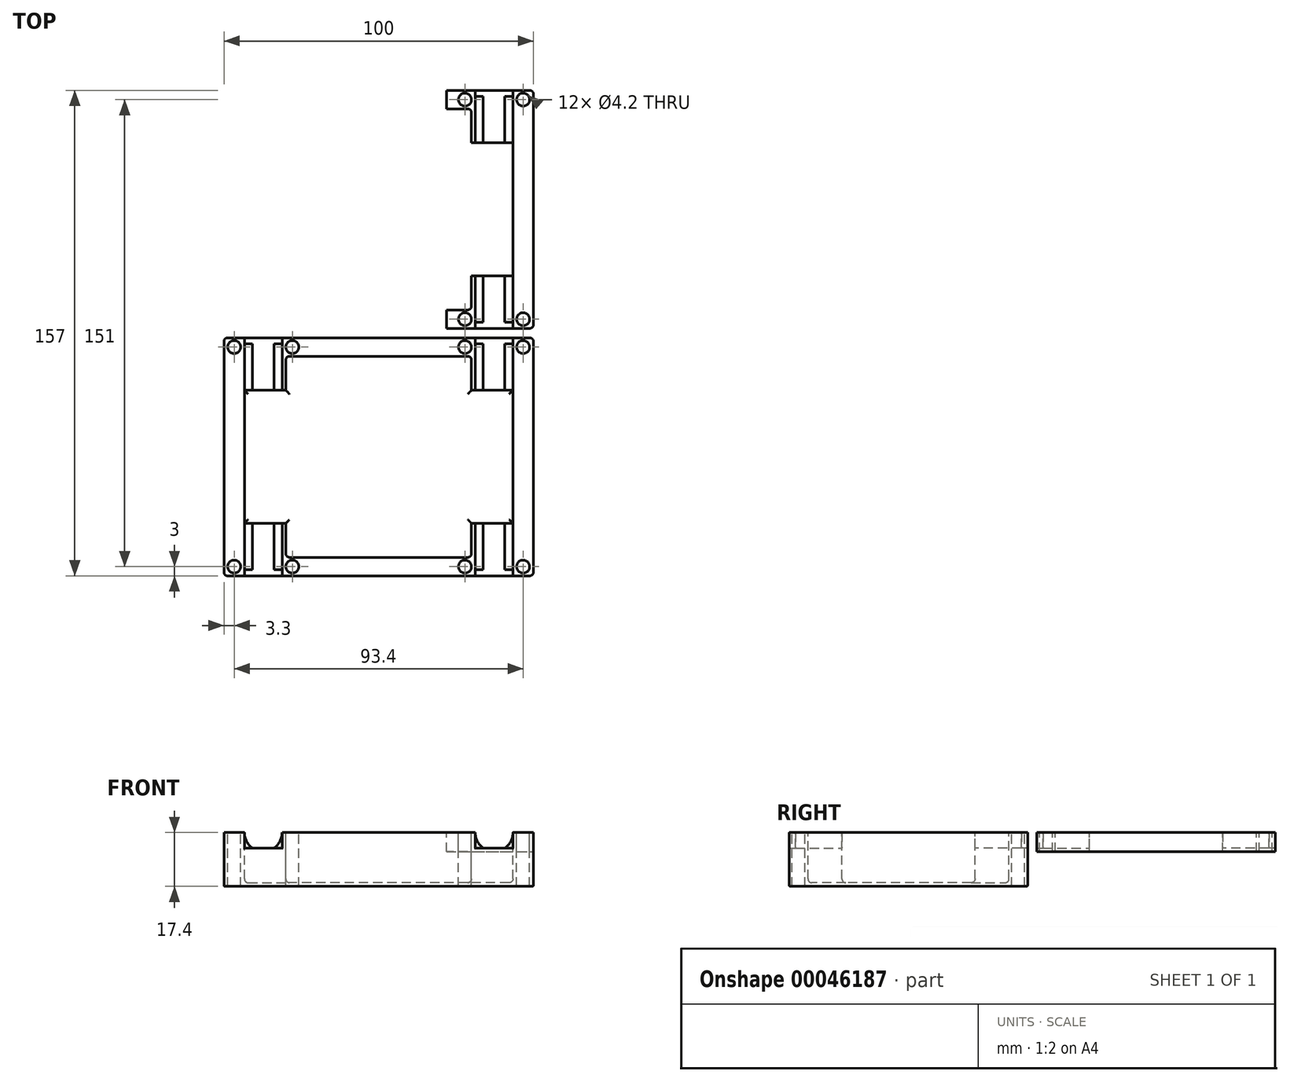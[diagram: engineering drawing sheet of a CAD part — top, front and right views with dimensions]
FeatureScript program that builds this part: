
annotation { "Feature Type Name" : "Feature", "Feature Type Description" : "" }
export const myFeature = defineFeature(function(context is Context, id is Id, definition is map)
    precondition{}
    {
        {
            var Q0;
            Q0=qCreatedBy(makeId("Top.planeOp"),FACE);
            var sketch = newSketch(context, id + "F0", { "sketchPlane" : qUnion([Q0])});
            skLineSegment(sketch, "E0.bottom", {"start": v(0, 0) * mm, "end": v(-30, 0) * mm});
            skLineSegment(sketch, "E0.top", {"start": v(0, 32.5) * mm, "end": v(-30, 32.5) * mm});
            skLineSegment(sketch, "E0.left", {"start": v(0, 0) * mm, "end": v(0, 32.5) * mm});
            skLineSegment(sketch, "E0.right", {"start": v(-30, 0) * mm, "end": v(-30, 32.5) * mm});
            skLineSegment(sketch, "E1", {"start": v(0, 32.5) * mm, "end": v(0, 38.5) * mm});
            skLineSegment(sketch, "E2", {"start": v(0, 38.5) * mm, "end": v(-50, 38.5) * mm});
            skLineSegment(sketch, "E3", {"start": v(-50, 38.5) * mm, "end": v(-50, 0) * mm});
            skLineSegment(sketch, "E4", {"start": v(-50, 0) * mm, "end": v(-30, 0) * mm});
            skLineSegment(sketch, "E5", {"start": v(-30, 32.5) * mm, "end": v(-30, 38.5) * mm});
            skLineSegment(sketch, "E6", {"start": v(-31.2, 38.5) * mm, "end": v(-31.2, 0) * mm});
            skLineSegment(sketch, "E7", {"start": v(-43.4, 38.5) * mm, "end": v(-43.4, 0) * mm});
            skLineSegment(sketch, "E8.bottom", {"start": v(-43.4, 36.5) * mm, "end": v(-31.2, 36.5) * mm});
            skLineSegment(sketch, "E8.top", {"start": v(-43.4, 21.5) * mm, "end": v(-31.2, 21.5) * mm});
            skLineSegment(sketch, "E8.left", {"start": v(-43.4, 36.5) * mm, "end": v(-43.4, 21.5) * mm});
            skLineSegment(sketch, "E8.right", {"start": v(-31.2, 36.5) * mm, "end": v(-31.2, 21.5) * mm});
            skLineSegment(sketch, "E9", {"start": v(-27.9, 38.5) * mm, "end": v(-27.9, 32.5) * mm, "construction": true});
            skCircle(sketch, "E10", {"center": v(-27.9, 35.5) * mm, "radius": 2.1 * mm});
            skLineSegment(sketch, "E11", {"start": v(-27.9, 35.5) * mm, "end": v(-50, 35.5) * mm, "construction": true});
            skLineSegment(sketch, "E12", {"start": v(-46.7, 38.5) * mm, "end": v(-46.7, 35.5) * mm, "construction": true});
            skCircle(sketch, "E13", {"center": v(-46.7, 35.5) * mm, "radius": 2.1 * mm});
            skSolve(sketch);
        }
        {
            var Q0;
            {var subQ1=sQuery(id+"F0.wireOp",EDGE,"E0.top");Q0=makeQuery(id+"F0.imprint","IMPRINT",FACE,{"disambiguationData":[TD([[makeQuery(id+"F0.imprint","IMPRINT",EDGE,{"derivedFrom":subQ1}),-1.0]])]});}
            var Q1;
            Q1=makeQuery(id+"F0.imprint","IMPRINT",FACE,{"disambiguationData":[TD([[makeQuery(id+"F0.imprint","IMPRINT",EDGE,{"derivedFrom":sQuery(id+"F0.wireOp",EDGE,"E0.bottom")}),-1.0]])]});
            var Q2;
            {var subQ5=sQuery(id+"F0.wireOp",EDGE,"E8.top");Q2=makeQuery(id+"F0.imprint","IMPRINT",FACE,{"disambiguationData":[TD([[makeQuery(id+"F0.imprint","IMPRINT",EDGE,{"derivedFrom":subQ5}),-1.0]])]});}
            var Q3;
            {var subQ5=sQuery(id+"F0.wireOp",EDGE,"E3");Q3=makeQuery(id+"F0.imprint","IMPRINT",FACE,{"disambiguationData":[TD([[makeQuery(id+"F0.imprint","IMPRINT",EDGE,{"derivedFrom":subQ5}),1.0]])]});}
            var Q4;
            Q4=makeQuery(id+"F0.imprint","IMPRINT",FACE,{"disambiguationData":[TD([[makeQuery(id+"F0.imprint","IMPRINT",EDGE,{"derivedFrom":sQuery(id+"F0.wireOp",EDGE,"E8.bottom")}),-1.0]])]});
            var Q5;
            {var subQ5=sQuery(id+"F0.wireOp",EDGE,"E8.bottom");Q5=makeQuery(id+"F0.imprint","IMPRINT",FACE,{"disambiguationData":[TD([[makeQuery(id+"F0.imprint","IMPRINT",EDGE,{"derivedFrom":subQ5}),1.0]])]});}
            var Q6;
            {var subQ1=sQuery(id+"F0.wireOp",EDGE,"E0.right");Q6=makeQuery(id+"F0.imprint","IMPRINT",FACE,{"disambiguationData":[TD([[makeQuery(id+"F0.imprint","IMPRINT",EDGE,{"derivedFrom":subQ1}),1.0]])]});}
            extrude(context, id + "F1", {"entities" : qUnion([Q0, Q1, Q2, Q3, Q4, Q5, Q6]), "oppositeDirection" : true, "depth" : 12.4 * mm});
        }
        {
            var Q0;
            Q0=makeQuery(id+"F0.imprint","IMPRINT",FACE,{"disambiguationData":[TD([[makeQuery(id+"F0.imprint","IMPRINT",EDGE,{"derivedFrom":sQuery(id+"F0.wireOp",EDGE,"E0.bottom")}),-1.0]])]});
            var Q1;
            {var subQ5=sQuery(id+"F0.wireOp",EDGE,"E8.top");Q1=makeQuery(id+"F0.imprint","IMPRINT",FACE,{"disambiguationData":[TD([[makeQuery(id+"F0.imprint","IMPRINT",EDGE,{"derivedFrom":subQ5}),-1.0]])]});}
            extrude(context, id + "F2", {"entities" : qUnion([Q0, Q1]), "operationType" : NewBodyOperationType.REMOVE, "oppositeDirection" : true, "depth" : 11.2 * mm});
        }
        {
            var Q0;
            {var subQ1=sQuery(id+"F0.wireOp",EDGE,"E0.top");Q0=makeQuery(id+"F0.imprint","IMPRINT",FACE,{"disambiguationData":[TD([[makeQuery(id+"F0.imprint","IMPRINT",EDGE,{"derivedFrom":subQ1}),-1.0]])]});}
            var Q1;
            {var subQ1=sQuery(id+"F0.wireOp",EDGE,"E0.right");Q1=makeQuery(id+"F0.imprint","IMPRINT",FACE,{"disambiguationData":[TD([[makeQuery(id+"F0.imprint","IMPRINT",EDGE,{"derivedFrom":subQ1}),1.0]])]});}
            var Q2;
            {var subQ5=sQuery(id+"F0.wireOp",EDGE,"E3");Q2=makeQuery(id+"F0.imprint","IMPRINT",FACE,{"disambiguationData":[TD([[makeQuery(id+"F0.imprint","IMPRINT",EDGE,{"derivedFrom":subQ5}),1.0]])]});}
            extrude(context, id + "F3", {"entities" : qUnion([Q0, Q1, Q2]), "operationType" : NewBodyOperationType.ADD, "depth" : 5 * mm});
        }
        {
            var Q0;
            {var subQ0=sQuery(id+"F0.wireOp",EDGE,"E6");Q0=makeQuery(id+"F3.boolean.opBoolean","MERGE",FACE,{"derivedFrom":[makeQuery(id+"F2.boolean.opBoolean","COPY",FACE,{"derivedFrom":makeQuery(id+"F2.opExtrude","SWEPT_FACE",FACE,{"disambiguationData":[OSD([subQ0])]})}),makeQuery(id+"F3.opExtrude","SWEPT_FACE",FACE,{"disambiguationData":[OSD([subQ0,sQuery(id+"F0.wireOp",EDGE,"E8.right")])]})]});}
            var sketch = newSketch(context, id + "F4", { "sketchPlane" : qUnion([Q0])});
            skLineSegment(sketch, "E14", {"start": v(-21.5, -11.2) * mm, "end": v(-21.5, 5) * mm});
            skSolve(sketch);
        }
        {
            var Q0;
            {var subQ2=sQuery(id+"F0.wireOp",EDGE,"E6");var subQ8=makeQuery(id+"F2.boolean.opBoolean","COPY",EDGE,{"derivedFrom":makeQuery(id+"F2.opExtrude","CAP_EDGE",EDGE,{"disambiguationData":[OSD([subQ2])],"isStart":false})});Q0=makeQuery(id+"F4.imprint","IMPRINT",FACE,{"disambiguationData":[TD([[makeQuery(id+"F4.imprint","IMPRINT",EDGE,{"derivedFrom":subQ8}),1.0]])]});}
            extrude(context, id + "F5", {"entities" : qUnion([Q0]), "operationType" : NewBodyOperationType.REMOVE, "endBound" : BoundingType.UP_TO_NEXT, "oppositeDirection" : true, "depth" : 25 * mm});
        }
        {
            var Q0;
            Q0=makeQuery(id+"F5.boolean.opBoolean","MERGE",FACE,{"derivedFrom":[makeQuery(id+"F2.boolean.opBoolean","COPY",FACE,{"derivedFrom":makeQuery(id+"F2.opExtrude","SWEPT_FACE",FACE,{"disambiguationData":[OSD([sQuery(id+"F0.wireOp",EDGE,"E8.top")])]})}),makeQuery(id+"F5.opExtrude","SWEPT_FACE",FACE,{"disambiguationData":[OSD([sQuery(id+"F4.wireOp",EDGE,"E14")])]})]});
            var sketch = newSketch(context, id + "F6", { "sketchPlane" : qUnion([Q0])});
            skLineSegment(sketch, "E15.0", {"start": v(-43.4, -11.2) * mm, "end": v(-43.4, 5) * mm, "construction": true});
            skLineSegment(sketch, "E16.0", {"start": v(-31.2, 0) * mm, "end": v(-31.2, 5) * mm, "construction": true});
            skLineSegment(sketch, "E17", {"start": v(-43.4, 5) * mm, "end": v(-31.2, 5) * mm, "construction": true});
            skArc(sketch, "E18", {"start": v(-43.4, 5) * mm, "mid": v(-42.7, 2.18) * mm, "end": v(-40.8, 0) * mm});
            skLineSegment(sketch, "E19.0", {"start": v(-43.4, 0) * mm, "end": v(-31.2, 0) * mm});
            skArc(sketch, "E20.trimOffspring", {"start": v(-33.8, 0) * mm, "mid": v(-31.9, 2.18) * mm, "end": v(-31.2, 5) * mm});
            skLineSegment(sketch, "E21", {"start": v(-43.4, 0) * mm, "end": v(-43.4, 5) * mm});
            skLineSegment(sketch, "E22", {"start": v(-31.2, 5) * mm, "end": v(-31.2, 0) * mm});
            skSolve(sketch);
        }
        {
            var Q0;
            {var subQ2=sQuery(id+"F6.wireOp",EDGE,"E20.trimOffspring");Q0=makeQuery(id+"F6.imprint","IMPRINT",FACE,{"disambiguationData":[TD([[makeQuery(id+"F6.imprint","IMPRINT",EDGE,{"derivedFrom":subQ2}),-1.0]])]});}
            var Q1;
            {var subQ0=sQuery(id+"F6.wireOp",EDGE,"E18");Q1=makeQuery(id+"F6.imprint","IMPRINT",FACE,{"disambiguationData":[TD([[makeQuery(id+"F6.imprint","IMPRINT",EDGE,{"derivedFrom":subQ0}),-1.0]])]});}
            extrude(context, id + "F7", {"entities" : qUnion([Q0, Q1]), "operationType" : NewBodyOperationType.ADD, "oppositeDirection" : true, "depth" : 15 * mm});
        }
        {
            var Q0;
            Q0=makeQuery(id+"F2.boolean.opBoolean","COPY",EDGE,{"derivedFrom":makeQuery(id+"F2.opExtrude","CAP_EDGE",EDGE,{"disambiguationData":[OSD([sQuery(id+"F0.wireOp",EDGE,"E7")])],"isStart":false})});
            var Q1;
            {var subQ0=sQuery(id+"F0.wireOp",EDGE,"E8.top");Q1=makeQuery(id+"F5.boolean.opBoolean","MERGE",EDGE,{"derivedFrom":[makeQuery(id+"F2.boolean.opBoolean","COPY",EDGE,{"derivedFrom":makeQuery(id+"F2.opExtrude","CAP_EDGE",EDGE,{"disambiguationData":[OSD([subQ0])],"isStart":false})}),makeQuery(id+"F5.opExtrude","SWEPT_EDGE",EDGE,{"disambiguationData":[OSD([sQuery(id+"F0.wireOp",EDGE,"E6"),subQ0,sQuery(id+"F0.wireOp",EDGE,"E8.right"),sQuery(id+"F4.wireOp",EDGE,"E14")])]})]});}
            var Q2;
            {var subQ0=sQuery(id+"F0.wireOp",EDGE,"E5");var subQ1=sQuery(id+"F0.wireOp",EDGE,"E0.right");var subQ2=sQuery(id+"F0.wireOp",EDGE,"E0.top");Q2=makeQuery(id+"F3.boolean.opBoolean","MERGE",EDGE,{"derivedFrom":[makeQuery(id+"F2.boolean.opBoolean","COPY",EDGE,{"derivedFrom":makeQuery(id+"F2.opExtrude","SWEPT_EDGE",EDGE,{"disambiguationData":[OSD([subQ2,subQ1,subQ0])]})}),makeQuery(id+"F3.opExtrude","SWEPT_EDGE",EDGE,{"disambiguationData":[OSD([subQ2,subQ1,subQ0])]})]});}
            var Q3;
            {var subQ0=sQuery(id+"F0.wireOp",EDGE,"E3");var subQ1=sQuery(id+"F0.wireOp",EDGE,"E2");Q3=makeQuery(id+"F3.boolean.opBoolean","MERGE",EDGE,{"derivedFrom":[makeQuery(id+"F1.opExtrude","SWEPT_EDGE",EDGE,{"disambiguationData":[OSD([subQ1,subQ0])]}),makeQuery(id+"F3.opExtrude","SWEPT_EDGE",EDGE,{"disambiguationData":[OSD([subQ1,subQ0])]})]});}
            var Q4;
            Q4=makeQuery(id+"F2.boolean.opBoolean","COPY",EDGE,{"derivedFrom":makeQuery(id+"F2.opExtrude","CAP_EDGE",EDGE,{"disambiguationData":[OSD([sQuery(id+"F0.wireOp",EDGE,"E0.right")])],"isStart":false})});
            var Q5;
            Q5=makeQuery(id+"F2.boolean.opBoolean","COPY",EDGE,{"derivedFrom":makeQuery(id+"F2.opExtrude","CAP_EDGE",EDGE,{"disambiguationData":[OSD([sQuery(id+"F0.wireOp",EDGE,"E0.top")])],"isStart":false})});
            fillet(context, id + "F8", {"entities" : qUnion([Q0, Q1, Q2, Q3, Q4, Q5]), "radius" : 1.2 * mm, "tangentPropagation" : true, "allowEdgeOverflow" : false});
        }
        {
            var Q0;
            Q0=makeQuery(id+"F1.opExtrude","CAP_EDGE",EDGE,{"disambiguationData":[OSD([sQuery(id+"F0.wireOp",EDGE,"E3")])],"isStart":false});
            var Q1;
            Q1=makeQuery(id+"F3.opExtrude","SWEPT_EDGE",EDGE,{"disambiguationData":[OSD([sQuery(id+"F0.wireOp",EDGE,"E2"),sQuery(id+"F0.wireOp",EDGE,"E6")])]});
            var Q2;
            Q2=makeQuery(id+"F3.opExtrude","SWEPT_EDGE",EDGE,{"disambiguationData":[OSD([sQuery(id+"F0.wireOp",EDGE,"E2"),sQuery(id+"F0.wireOp",EDGE,"E7")])]});
            fillet(context, id + "F9", {"entities" : qUnion([Q0, Q1, Q2]), "radius" : .3 * mm, "tangentPropagation" : true, "allowEdgeOverflow" : false});
        }
        {
            var Q0;
            Q0=makeQuery(id+"F1.opExtrude","SWEPT_BODY",BODY,{"disambiguationData":[OSD([sQuery(id+"F0.wireOp",EDGE,"E0.bottom"),sQuery(id+"F0.wireOp",EDGE,"E0.left"),sQuery(id+"F0.wireOp",EDGE,"E1"),sQuery(id+"F0.wireOp",EDGE,"E2"),sQuery(id+"F0.wireOp",EDGE,"E3"),sQuery(id+"F0.wireOp",EDGE,"E4"),sQuery(id+"F0.wireOp",EDGE,"E10"),sQuery(id+"F0.wireOp",EDGE,"E13")])]});
            var Q1;
            {var subQ0=sQuery(id+"F0.wireOp",EDGE,"E4");var subQ1=sQuery(id+"F0.wireOp",EDGE,"E0.bottom");Q1=makeQuery(id+"F3.boolean.opBoolean","MERGE",FACE,{"derivedFrom":[makeQuery(id+"F1.opExtrude","SWEPT_FACE",FACE,{"disambiguationData":[OSD([subQ1,subQ0])]}),makeQuery(id+"F3.opExtrude","SWEPT_FACE",FACE,{"disambiguationData":[OSD([subQ0]),TDD([makeQuery(id+"F0.imprint","IMPRINT",EDGE,{"disambiguationData":[TD([[makeQuery(id+"F0.imprint","INTERSECT",VERTEX,{"derivedFrom":[sQuery(id+"F0.wireOp",EDGE,"E3"),subQ0]}),-1.0]])],"derivedFrom":subQ0})])]}),makeQuery(id+"F3.opExtrude","SWEPT_FACE",FACE,{"disambiguationData":[OSD([subQ0]),TDD([makeQuery(id+"F0.imprint","IMPRINT",EDGE,{"disambiguationData":[TD([[makeQuery(id+"F0.imprint","INTERSECT",VERTEX,{"derivedFrom":[subQ0,sQuery(id+"F0.wireOp",EDGE,"E6")]}),-1.0]])],"derivedFrom":subQ0})])]})]});}
            mirror(context, id + "F10", {"operationType" : NewBodyOperationType.ADD, "entities" : qUnion([Q0]), "mirrorPlane" : qUnion([Q1])});
        }
        {
            var Q0;
            Q0=makeQuery(id+"F1.opExtrude","SWEPT_BODY",BODY,{"disambiguationData":[OSD([sQuery(id+"F0.wireOp",EDGE,"E0.bottom"),sQuery(id+"F0.wireOp",EDGE,"E0.left"),sQuery(id+"F0.wireOp",EDGE,"E1"),sQuery(id+"F0.wireOp",EDGE,"E2"),sQuery(id+"F0.wireOp",EDGE,"E3"),sQuery(id+"F0.wireOp",EDGE,"E4"),sQuery(id+"F0.wireOp",EDGE,"E10"),sQuery(id+"F0.wireOp",EDGE,"E13")])]});
            var Q1;
            {var subQ0=sQuery(id+"F0.wireOp",EDGE,"E1");var subQ1=makeQuery(id+"F3.boolean.opBoolean","MERGE",FACE,{"derivedFrom":[makeQuery(id+"F1.opExtrude","SWEPT_FACE",FACE,{"disambiguationData":[OSD([sQuery(id+"F0.wireOp",EDGE,"E0.left"),subQ0])]}),makeQuery(id+"F3.opExtrude","SWEPT_FACE",FACE,{"disambiguationData":[OSD([subQ0])]})]});Q1=makeQuery(id+"F10.boolean.opBoolean","MERGE",FACE,{"derivedFrom":[subQ1,makeQuery(id+"F10.opPattern","COPY",FACE,{"derivedFrom":subQ1,"instanceName":"1"})]});}
            mirror(context, id + "F11", {"operationType" : NewBodyOperationType.ADD, "entities" : qUnion([Q0]), "mirrorPlane" : qUnion([Q1])});
        }
        {
            var Q0;
            Q0=makeQuery(id+"F1.opExtrude","SWEPT_BODY",BODY,{"disambiguationData":[OSD([sQuery(id+"F0.wireOp",EDGE,"E0.bottom"),sQuery(id+"F0.wireOp",EDGE,"E0.left"),sQuery(id+"F0.wireOp",EDGE,"E1"),sQuery(id+"F0.wireOp",EDGE,"E2"),sQuery(id+"F0.wireOp",EDGE,"E3"),sQuery(id+"F0.wireOp",EDGE,"E4"),sQuery(id+"F0.wireOp",EDGE,"E10"),sQuery(id+"F0.wireOp",EDGE,"E13")])]});
            transform(context, id + "F12", {"entities" : qUnion([Q0]), "transformType" : TransformType.TRANSLATION_3D, "dx" : 0 * mm, "dy" : 80 * mm, "dz" : 0 * mm, "makeCopy" : true});
        }
        {
            var Q0;
            {var subQ0=sQuery(id+"F0.wireOp",EDGE,"E2");var subQ1=makeQuery(id+"F0.imprint","INTERSECT",VERTEX,{"derivedFrom":[subQ0,sQuery(id+"F0.wireOp",EDGE,"E5")]});var subQ2=makeQuery(id+"F10.opPattern","COPY",FACE,{"derivedFrom":makeQuery(id+"F3.boolean.opBoolean","MERGE",FACE,{"derivedFrom":[makeQuery(id+"F1.opExtrude","SWEPT_FACE",FACE,{"disambiguationData":[OSD([subQ0])]}),makeQuery(id+"F3.opExtrude","SWEPT_FACE",FACE,{"disambiguationData":[OSD([subQ0]),TDD([makeQuery(id+"F0.imprint","IMPRINT",EDGE,{"disambiguationData":[TD([[makeQuery(id+"F0.imprint","INTERSECT",VERTEX,{"derivedFrom":[sQuery(id+"F0.wireOp",EDGE,"E1"),subQ0]}),-1.0]])],"derivedFrom":subQ0}),makeQuery(id+"F0.imprint","IMPRINT",EDGE,{"disambiguationData":[TD([[subQ1,-1.0]])],"derivedFrom":subQ0})])]}),makeQuery(id+"F3.opExtrude","SWEPT_FACE",FACE,{"disambiguationData":[OSD([subQ0]),TDD([makeQuery(id+"F0.imprint","IMPRINT",EDGE,{"disambiguationData":[TD([[makeQuery(id+"F0.imprint","INTERSECT",VERTEX,{"derivedFrom":[subQ0,sQuery(id+"F0.wireOp",EDGE,"E3")]}),1.0]])],"derivedFrom":subQ0})])]})]}),"instanceName":"1"});Q0=makeQuery(id+"F12.opPattern","COPY",FACE,{"derivedFrom":makeQuery(id+"F11.boolean.opBoolean","MERGE",FACE,{"derivedFrom":[subQ2,makeQuery(id+"F11.opPattern","COPY",FACE,{"derivedFrom":subQ2,"instanceName":"1"})]}),"instanceName":"1"});}
            var sketch = newSketch(context, id + "F13", { "sketchPlane" : qUnion([Q0])});
            skLineSegment(sketch, "E23.0", {"start": v(50, 5) * mm, "end": v(50, -12.1) * mm});
            skLineSegment(sketch, "E24.0", {"start": v(-48.8, -12.4) * mm, "end": v(48.8, -12.4) * mm});
            skLineSegment(sketch, "E25", {"start": v(22, -1.2) * mm, "end": v(50, -1.2) * mm});
            skLineSegment(sketch, "E26", {"start": v(22, -1.2) * mm, "end": v(22, -12.4) * mm});
            skLineSegment(sketch, "E27", {"start": v(22, -12.4) * mm, "end": v(50, -12.4) * mm});
            skLineSegment(sketch, "E28", {"start": v(50, -12.4) * mm, "end": v(50, -12.1) * mm});
            skLineSegment(sketch, "E29.0", {"start": v(30.9, 0) * mm, "end": v(43.7, 0) * mm});
            skLineSegment(sketch, "E30", {"start": v(22, -1.2) * mm, "end": v(22, 5) * mm});
            skLineSegment(sketch, "E31.0", {"start": v(-50, 5) * mm, "end": v(-50, -12.1) * mm});
            skLineSegment(sketch, "E32", {"start": v(-50, 5) * mm, "end": v(22, 5) * mm});
            skLineSegment(sketch, "E33", {"start": v(-48.8, -12.4) * mm, "end": v(-50, -12.4) * mm});
            skLineSegment(sketch, "E34", {"start": v(-50, -12.4) * mm, "end": v(-50, -12.1) * mm});
            skSolve(sketch);
        }
        {
            var Q0;
            Q0 = qSketchRegion(id + "F13", true);
            var Q1;
            {var subQ0=sQuery(id+"F0.wireOp",EDGE,"E2");var subQ1=makeQuery(id+"F0.imprint","INTERSECT",VERTEX,{"derivedFrom":[subQ0,sQuery(id+"F0.wireOp",EDGE,"E5")]});var subQ2=makeQuery(id+"F3.boolean.opBoolean","MERGE",FACE,{"derivedFrom":[makeQuery(id+"F1.opExtrude","SWEPT_FACE",FACE,{"disambiguationData":[OSD([subQ0])]}),makeQuery(id+"F3.opExtrude","SWEPT_FACE",FACE,{"disambiguationData":[OSD([subQ0]),TDD([makeQuery(id+"F0.imprint","IMPRINT",EDGE,{"disambiguationData":[TD([[makeQuery(id+"F0.imprint","INTERSECT",VERTEX,{"derivedFrom":[sQuery(id+"F0.wireOp",EDGE,"E1"),subQ0]}),-1.0]])],"derivedFrom":subQ0}),makeQuery(id+"F0.imprint","IMPRINT",EDGE,{"disambiguationData":[TD([[subQ1,-1.0]])],"derivedFrom":subQ0})])]}),makeQuery(id+"F3.opExtrude","SWEPT_FACE",FACE,{"disambiguationData":[OSD([subQ0]),TDD([makeQuery(id+"F0.imprint","IMPRINT",EDGE,{"disambiguationData":[TD([[makeQuery(id+"F0.imprint","INTERSECT",VERTEX,{"derivedFrom":[subQ0,sQuery(id+"F0.wireOp",EDGE,"E3")]}),1.0]])],"derivedFrom":subQ0})])]})]});Q1=makeQuery(id+"F12.opPattern","COPY",FACE,{"derivedFrom":makeQuery(id+"F11.boolean.opBoolean","MERGE",FACE,{"derivedFrom":[subQ2,makeQuery(id+"F11.opPattern","COPY",FACE,{"derivedFrom":subQ2,"instanceName":"1"})]}),"instanceName":"1"});}
            extrude(context, id + "F14", {"entities" : qUnion([Q0]), "operationType" : NewBodyOperationType.REMOVE, "endBound" : BoundingType.UP_TO_SURFACE, "oppositeDirection" : true, "endBoundEntityFace" : qUnion([Q1]), "depth" : 25 * mm});
        }
    });
